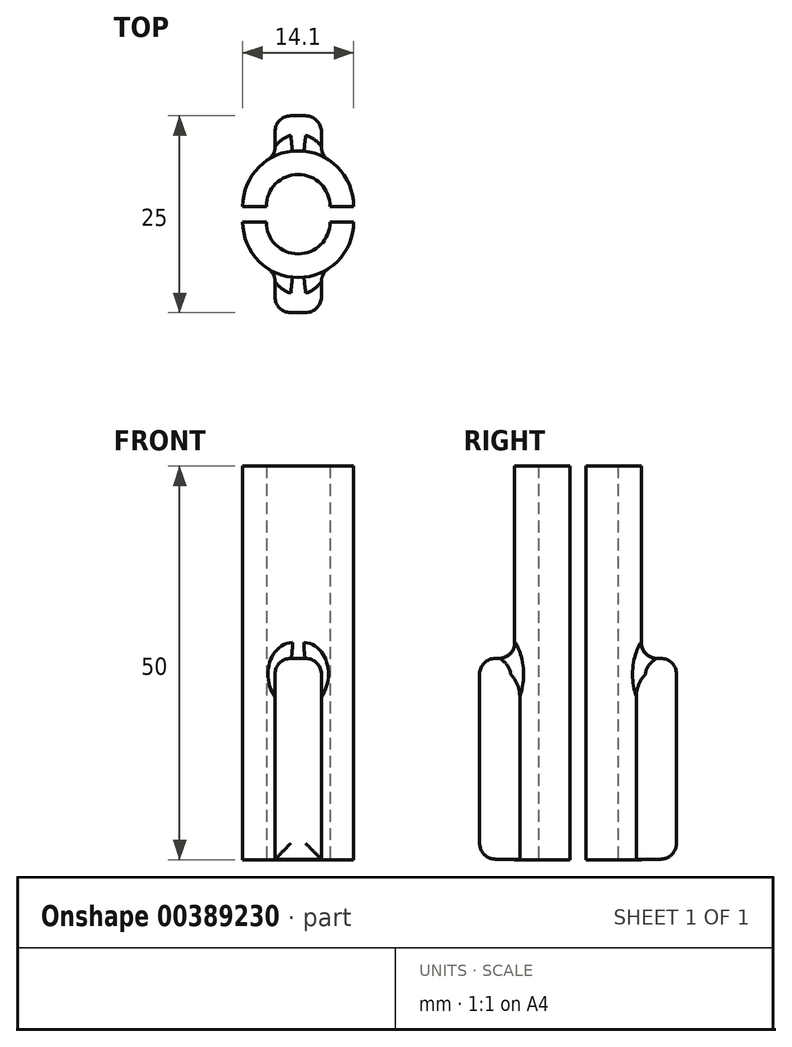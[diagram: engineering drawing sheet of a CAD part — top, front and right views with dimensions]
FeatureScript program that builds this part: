
annotation { "Feature Type Name" : "Feature", "Feature Type Description" : "" }
export const myFeature = defineFeature(function(context is Context, id is Id, definition is map)
    precondition{}
    {
        {
            var Q0;
            Q0=qCreatedBy(makeId("Top.planeOp"),FACE);
            var sketch = newSketch(context, id + "F0", { "sketchPlane" : qUnion([Q0])});
            skLineSegment(sketch, "E0", {"start": v(7, 0.87) * mm, "end": v(7, 0.87) * mm});
            skArc(sketch, "E1", {"start": v(-4.05, 0) * mm, "mid": v(0, -4.05) * mm, "end": v(4.05, 0) * mm});
            skArc(sketch, "E2", {"start": v(-7.05, 0) * mm, "mid": v(0, -7.05) * mm, "end": v(7.05, 0) * mm});
            skLineSegment(sketch, "E3", {"start": v(7.05, 0) * mm, "end": v(-7.05, 0) * mm});
            skPoint(sketch, "E4.start.orphan", {"position": v(-4.01, 0.55) * mm});
            skPoint(sketch, "E5.end.orphan", {"position": v(4.01, 0.55) * mm});
            skPoint(sketch, "E6.orphan", {"position": v(8.16, 0) * mm});
            skSolve(sketch);
        }
        {
            var Q0;
            Q0=makeQuery(id+"F0.imprint","IMPRINT",FACE,{"disambiguationData":[TD([[makeQuery(id+"F0.imprint","IMPRINT",EDGE,{"derivedFrom":sQuery(id+"F0.wireOp",EDGE,"E4")}),1.0]])]});
            var Q1;
            {var subQ0=sQuery(id+"F0.wireOp",EDGE,"E1");Q1=makeQuery(id+"F0.imprint","IMPRINT",FACE,{"disambiguationData":[TD([[makeQuery(id+"F0.imprint","IMPRINT",EDGE,{"derivedFrom":subQ0}),-1.0]])]});}
            extrude(context, id + "F1", {"entities" : qUnion([Q0, Q1]), "depth" : 50 * mm});
        }
        {
            var Q0;
            Q0=qCreatedBy(makeId("Front.planeOp"),FACE);
            var sketch = newSketch(context, id + "F2", { "sketchPlane" : qUnion([Q0])});
            skLineSegment(sketch, "E7", {"start": v(-7.05, 0) * mm, "end": v(-7.05, 50) * mm});
            skLineSegment(sketch, "E8.bottom", {"start": v(-2.94, 25.57) * mm, "end": v(2.94, 25.57) * mm});
            skLineSegment(sketch, "E8.top", {"start": v(-2.94, 0.07) * mm, "end": v(2.94, 0.07) * mm});
            skLineSegment(sketch, "E8.left", {"start": v(-2.94, 25.57) * mm, "end": v(-2.94, 0.07) * mm});
            skLineSegment(sketch, "E8.right", {"start": v(2.94, 25.57) * mm, "end": v(2.94, 0.07) * mm});
            skPoint(sketch, "E8.middle", {"position": v(0, 12.82) * mm});
            skSolve(sketch);
        }
        {
            var Q0;
            Q0=qSketchRegion(id+"F2",true);
            extrude(context, id + "F3", {"entities" : qUnion([Q0]), "operationType" : NewBodyOperationType.ADD, "depth" : 11.5 * mm});
        }
        {
            var Q0;
            {var subQ2=sQuery(id+"F2.wireOp",EDGE,"E8.bottom");Q0=makeQuery(id+"F3.boolean.opBoolean","SPLIT",FACE,{"disambiguationData":[TD([makeQuery(id+"F1.opExtrude","SWEPT_FACE",FACE,{"disambiguationData":[OSD([sQuery(id+"F0.wireOp",EDGE,"E1")])]})])],"derivedFrom":makeQuery(id+"F3.opExtrude","SWEPT_FACE",FACE,{"disambiguationData":[OSD([subQ2])]})});}
            extrude(context, id + "F4", {"entities" : qUnion([Q0]), "operationType" : NewBodyOperationType.REMOVE, "endBound" : BoundingType.THROUGH_ALL, "oppositeDirection" : true, "depth" : 25 * mm});
        }
        {
            var Q0;
            {var subQ2=sQuery(id+"F2.wireOp",EDGE,"E8.bottom");Q0=makeQuery(id+"F3.boolean.opBoolean","SPLIT",FACE,{"disambiguationData":[TD([makeQuery(id+"F1.opExtrude","SWEPT_FACE",FACE,{"disambiguationData":[OSD([sQuery(id+"F0.wireOp",EDGE,"E2")])]})])],"derivedFrom":makeQuery(id+"F3.opExtrude","SWEPT_FACE",FACE,{"disambiguationData":[OSD([subQ2])]})});}
            var Q1;
            Q1=makeQuery(id+"F3.opExtrude","CAP_FACE",FACE,{"disambiguationData":[OSD([sQuery(id+"F2.wireOp",EDGE,"E8.bottom"),sQuery(id+"F2.wireOp",EDGE,"E8.top"),sQuery(id+"F2.wireOp",EDGE,"E8.left"),sQuery(id+"F2.wireOp",EDGE,"E8.right")])],"isStart":false});
            fillet(context, id + "F5", {"entities" : qUnion([Q0, Q1]), "radius" : 2 * mm, "tangentPropagation" : true, "allowEdgeOverflow" : false});
        }
        {
            var Q0;
            Q0=qCreatedBy(makeId("Front.planeOp"),FACE);
            cPlane(context, id + "F6", {"entities" : qUnion([Q0]), "cplaneType" : CPlaneType.OFFSET, "offset" : 1 * mm, "oppositeDirection" : true, "width" : 150 * mm, "height" : 150 * mm});
        }
        {
            var Q0;
            Q0=makeQuery(id+"F1.opExtrude","SWEPT_BODY",BODY,{"disambiguationData":[OSD([sQuery(id+"F0.wireOp",EDGE,"E1"),sQuery(id+"F0.wireOp",EDGE,"E2"),sQuery(id+"F0.wireOp",EDGE,"E3")])]});
            var Q1;
            Q1=qCreatedBy(id+"F6.planeOp",FACE);
            mirror(context, id + "F7", {"entities" : qUnion([Q0]), "mirrorPlane" : qUnion([Q1])});
        }
    });
